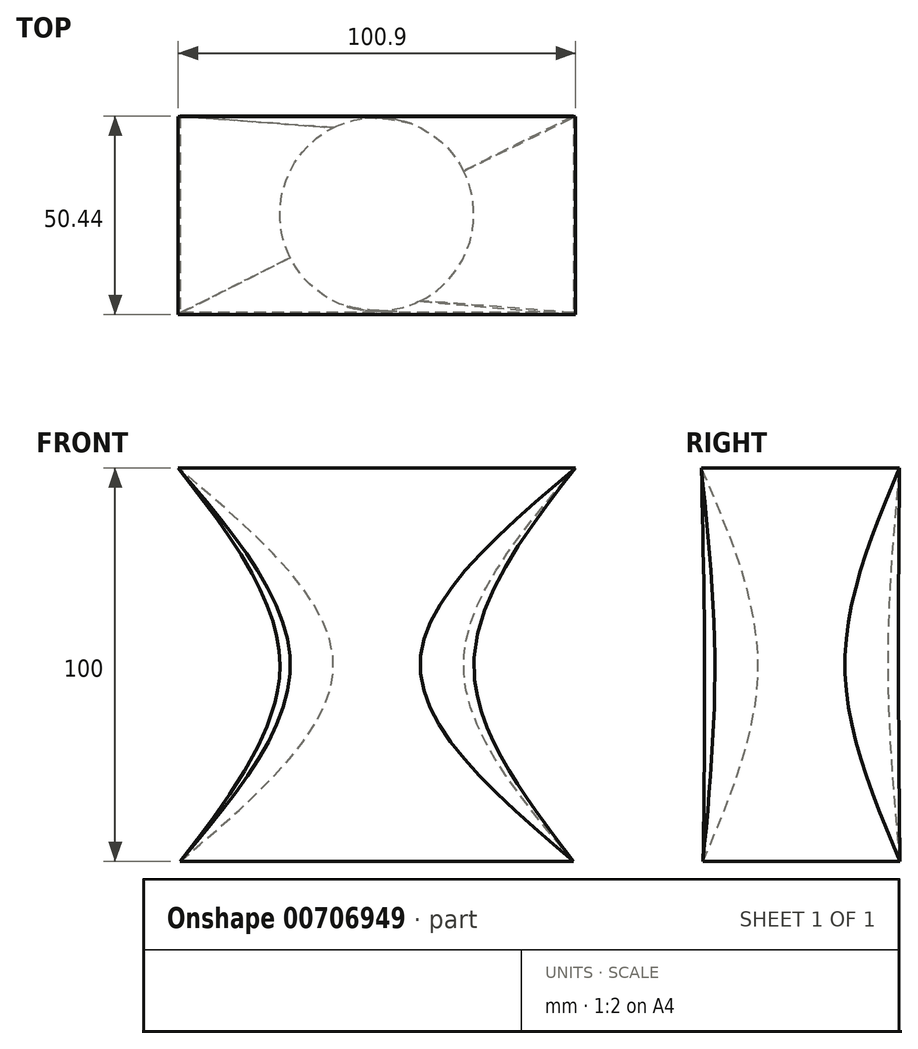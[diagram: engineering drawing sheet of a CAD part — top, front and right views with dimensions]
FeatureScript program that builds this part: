
annotation { "Feature Type Name" : "Feature", "Feature Type Description" : "" }
export const myFeature = defineFeature(function(context is Context, id is Id, definition is map)
    precondition{}
    {
        {
            var Q0;
            Q0=qCreatedBy(makeId("Top.planeOp"),FACE);
            var sketch = newSketch(context, id + "F0", { "sketchPlane" : qUnion([Q0])});
            skLineSegment(sketch, "E0.bottom", {"start": v(50, 25) * mm, "end": v(-50, 25) * mm});
            skLineSegment(sketch, "E0.top", {"start": v(50, -25) * mm, "end": v(-50, -25) * mm});
            skLineSegment(sketch, "E0.left", {"start": v(50, 25) * mm, "end": v(50, -25) * mm});
            skLineSegment(sketch, "E0.right", {"start": v(-50, 25) * mm, "end": v(-50, -25) * mm});
            skPoint(sketch, "E0.middle", {"position": v(0, 0) * mm});
            skSolve(sketch);
        }
        {
            var Q0;
            Q0=qCreatedBy(makeId("Top.planeOp"),FACE);
            cPlane(context, id + "F1", {"entities" : qUnion([Q0]), "cplaneType" : CPlaneType.OFFSET, "offset" : 50 * mm, "width" : 150 * mm, "height" : 150 * mm});
        }
        {
            var Q0;
            Q0=qCreatedBy(id+"F1.planeOp",FACE);
            cPlane(context, id + "F2", {"entities" : qUnion([Q0]), "cplaneType" : CPlaneType.OFFSET, "offset" : 50 * mm, "width" : 150 * mm, "height" : 150 * mm});
        }
        {
            var Q0;
            Q0=qCreatedBy(id+"F2.planeOp",FACE);
            var sketch = newSketch(context, id + "F3", { "sketchPlane" : qUnion([Q0])});
            skLineSegment(sketch, "E1.bottom", {"start": v(-50.45, -25.44) * mm, "end": v(50.45, -25.44) * mm});
            skLineSegment(sketch, "E1.top", {"start": v(-50.45, 24.88) * mm, "end": v(50.45, 24.88) * mm});
            skLineSegment(sketch, "E1.left", {"start": v(-50.45, -25.44) * mm, "end": v(-50.45, 24.88) * mm});
            skLineSegment(sketch, "E1.right", {"start": v(50.45, -25.44) * mm, "end": v(50.45, 24.88) * mm});
            skSolve(sketch);
        }
        {
            var Q0;
            Q0=qCreatedBy(id+"F1.planeOp",FACE);
            var sketch = newSketch(context, id + "F4", { "sketchPlane" : qUnion([Q0])});
            skCircle(sketch, "E2", {"center": v(0, 0) * mm, "radius": 24.63 * mm});
            skSolve(sketch);
        }
        {
            var Q0;
            Q0=makeQuery(id+"F0.imprint","IMPRINT",FACE,{"disambiguationData":[TD([[makeQuery(id+"F0.imprint","IMPRINT",EDGE,{"derivedFrom":sQuery(id+"F0.wireOp",EDGE,"E0.bottom")}),1.0]])]});
            var Q1;
            Q1=makeQuery(id+"F4.imprint","IMPRINT",FACE,{"disambiguationData":[TD([[makeQuery(id+"F4.imprint","IMPRINT",EDGE,{"derivedFrom":sQuery(id+"F4.wireOp",EDGE,"E2")}),1.0]])]});
            var Q2;
            Q2=makeQuery(id+"F3.imprint","IMPRINT",FACE,{"disambiguationData":[TD([[makeQuery(id+"F3.imprint","IMPRINT",EDGE,{"derivedFrom":sQuery(id+"F3.wireOp",EDGE,"E1.bottom")}),1.0]])]});
            loft(context, id + "F5", {"sheetProfilesArray" : [{ "sheetProfileEntities" : qUnion([Q0]) }, { "sheetProfileEntities" : qUnion([Q1]) }, { "sheetProfileEntities" : qUnion([Q2]) }]});
        }
    });
